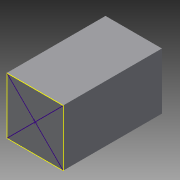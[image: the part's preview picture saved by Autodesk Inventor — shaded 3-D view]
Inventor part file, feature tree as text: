
AUTODESK INVENTOR PART (.ipt)
format: ipt  version: 2013 (Build 170138000, 138)  size: 87,552 bytes
history: native  units: mm
features: sketch x3, other x1, extrude x1, revolve x1
ambient origin geometry x8: Origin, YZ Plane, XZ Plane, XY Plane, X Axis, Y Axis, Z Axis, Center Point
feature tree (6):
  other  "ソリッド1"
  extrude  "押し出し1"  Depth=20.0mm
  revolve  "回転1"
  sketch  "スケッチ3"
  sketch  "スケッチ1"
  sketch  "スケッチ2"
